FCSTD DOCUMENT  (FreeCAD 0.20R29177 +426 (Git))
Label: Spring
License: All rights reserved
LicenseURL: https://en.wikipedia.org/wiki/All_rights_reserved
objects: PartDesign::CoordinateSystem×2, PartDesign::Body×1, Part::Helix×1, Sketcher::SketchObject×1, PartDesign::AdditivePipe×1, App::Part×1
note: 7 computed .brp shape members not serialized (recipe doc carries the construction recipe); baked Part::Feature solids carry a one-line shape summary decoded from their .brp

FEATURE [PartDesign::Body] Body  label="SpringBody"
  Origin = -> Origin
FEATURE [Part::Helix] Helix
  Angle = 0
  AttacherType = Attacher::AttachEngine3D
  Height = 40
  LocalCoord = 0
  Pitch = 10
  Radius = 10
  SegmentLength = 0
  Style = 1
FEATURE [Sketcher::SketchObject] Sketch  label="ProfileSketch"
  FullyConstrained = false
  MapMode = 5
  Placement = pos=(0,0,0) rot=(1,0,0;1.5708rad)
  sketch-geometry (1):
    g0: Circle CenterX=9.98699 CenterY=0 CenterZ=0 NormalX=0 NormalY=0 NormalZ=1 AngleXU=0 Radius=2
  constraints (2):
    c: PointOnObject(g0,g-1)
    c: Diameter(g0) = 4
FEATURE [PartDesign::AdditivePipe] AdditivePipe
  AuxilleryCurvelinear = true
  AuxillerySpineTangent = false
  Binormal = (0,0,0)
  Mode = 0
  Placement = pos=(0,0,0) rot=(1,0,0;1.5708rad)
  Profile = -> Sketch
  Refine = true
  Spine = -> Helix
  SpineTangent = false
  Transformation = 0
  Transition = 0
FEATURE [PartDesign::CoordinateSystem] LCS_SqareWasher
  AttacherType = Attacher::AttachEngine3D
  MapMode = 45
  Placement = pos=(9.98699,0,0) rot=(0,0.707107,0.707107;3.14159rad)
  Support = -> [AdditivePipe]
FEATURE [PartDesign::CoordinateSystem] LCS_Head
  AttacherType = Attacher::AttachEngine3D
  Placement = pos=(-1.02332,6.74457,1.47352) rot=(-0.993163,-0.090928,0.073208;1.36241rad)
FEATURE [App::Part] Part  label="SpringPart"
  Group = -> [Body,Sketch,AdditivePipe,Helix,LCS_SqareWasher,LCS_Head]
  Origin = -> Origin001
